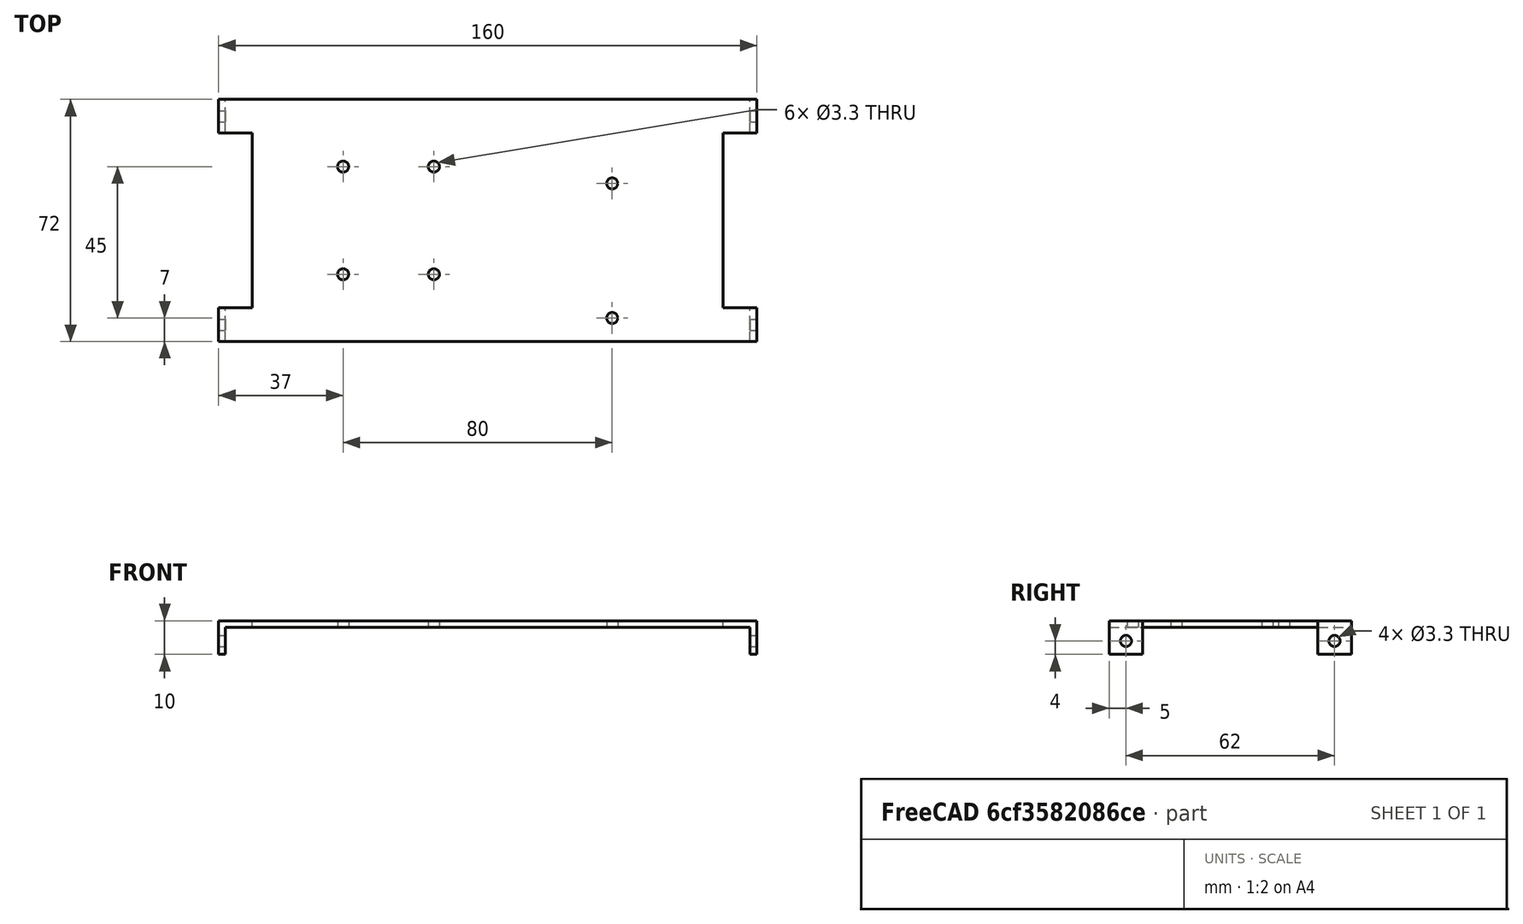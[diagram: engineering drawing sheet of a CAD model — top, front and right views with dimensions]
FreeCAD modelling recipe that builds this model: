
FCSTD DOCUMENT  (FreeCAD 0.17R13522 (Git))
Label: Zwischenblech_teensy
License: All rights reserved
LicenseURL: http://en.wikipedia.org/wiki/All_rights_reserved
objects: TechDraw::DrawViewDimension×22, Part::Box×3, Part::Cut×3, TechDraw::DrawProjGroupItem×3, Sketcher::SketchObject×2, PartDesign::Hole×2, Part::Mirroring×1, PartDesign::FeatureBase×1, TechDraw::DrawSVGTemplate×1, PartDesign::Body×1, TechDraw::DrawProjGroup×1, TechDraw::DrawPage×1
note: 15 computed .brp shape members not serialized (recipe doc carries the construction recipe); baked Part::Feature solids carry a one-line shape summary decoded from their .brp

FEATURE [Part::Box] Box  label="Würfel"
  AttacherType = Attacher::AttachEngine3D
  Height = 10
  Length = 160
  Width = 72
FEATURE [Part::Box] Box001  label="Würfel001"
  AttacherType = Attacher::AttachEngine3D
  Height = 10
  Length = 10
  Placement = pos=(0,10,0) rot=(0,0,1;0rad)
  Width = 52
FEATURE [Part::Mirroring] Part__Mirroring  label="Würfel001 (Mirror #1)"
  Base = (80,0,0)
  Normal = (1,0,0)
  Source = -> Box001
FEATURE [Part::Cut] Cut
  Base = -> Box
  Tool = -> Box001
FEATURE [Part::Cut] Cut001
  Base = -> Cut
  Tool = -> Part__Mirroring
FEATURE [Part::Box] Box002  label="Würfel002"
  AttacherType = Attacher::AttachEngine3D
  Height = 8
  Length = 156
  Placement = pos=(2,0,0) rot=(0,0,1;0rad)
  Width = 72
FEATURE [Part::Cut] Cut002
  Base = -> Cut001
  Tool = -> Box002
FEATURE [PartDesign::FeatureBase] BaseFeature
  BaseFeature = -> Cut002
FEATURE [Sketcher::SketchObject] Sketch
  MapMode = 5
  Placement = pos=(0,0,0) rot=(0.57735,-0.57735,-0.57735;2.0944rad)
  Support = -> [BaseFeature]
  sketch-geometry (2):
    g0: Circle CenterX=-5 CenterY=4 CenterZ=0 NormalX=0 NormalY=0 NormalZ=1 AngleXU=0 Radius=2.2
    g1: Circle CenterX=-67 CenterY=4 CenterZ=0 NormalX=0 NormalY=0 NormalZ=1 AngleXU=0 Radius=2.2
  constraints (6):
    c: Horizontal(g0,g1)
    c: DistanceY(g-1,g0) = 4
    c: Radius(g0) = 2.2
    c: Radius(g1) = 2.2
    c: DistanceX(g0,g-1) = 5
    c: DistanceX(g1,g-1) = 67
FEATURE [PartDesign::Hole] Hole
  BaseFeature = -> BaseFeature
  Depth = 25
  DepthType = 1
  Diameter = 3.3
  DrillPoint = 1
  DrillPointAngle = 118
  HoleCutCountersinkAngle = 90
  HoleCutDepth = 0
  HoleCutDiameter = 3
  HoleCutType = 0
  ModelActualThread = false
  Profile = -> Sketch
  Tapered = false
  TaperedAngle = 90
  ThreadAngle = 0
  ThreadClass = 0
  ThreadCutOffInner = 0
  ThreadCutOffOuter = 0
  ThreadDirection = 0
  ThreadFit = 0
  ThreadPitch = 0
  ThreadSize = 3
  ThreadType = 1
  Threaded = false
FEATURE [TechDraw::DrawSVGTemplate] Template
  EditableTexts = Designed_by_Name=Christian Dengler; FC-Date=25.04.2018; FC-SC=Scale; FC-SH=1/1; FC-Title=Zwischenblech, Mitte
  Height = 210
  Orientation = 1
  Width = 297
FEATURE [Sketcher::SketchObject] Sketch001
  MapMode = 5
  Placement = pos=(0,0,10) rot=(0,0,1;0rad)
  Support = -> [Hole]
  sketch-geometry (6):
    g0: Circle CenterX=37 CenterY=20 CenterZ=0 NormalX=0 NormalY=0 NormalZ=1 AngleXU=0 Radius=1.65
    g1: Circle CenterX=37 CenterY=52 CenterZ=0 NormalX=0 NormalY=0 NormalZ=1 AngleXU=0 Radius=1.65
    g2: Circle CenterX=64 CenterY=52 CenterZ=0 NormalX=0 NormalY=0 NormalZ=1 AngleXU=0 Radius=1.65
    g3: Circle CenterX=64 CenterY=20 CenterZ=0 NormalX=0 NormalY=0 NormalZ=1 AngleXU=0 Radius=1.65
    g4: Circle CenterX=117 CenterY=47 CenterZ=0 NormalX=0 NormalY=0 NormalZ=1 AngleXU=0 Radius=1.65
    g5: Circle CenterX=117 CenterY=7 CenterZ=0 NormalX=0 NormalY=0 NormalZ=1 AngleXU=0 Radius=1.65
  constraints (18):
    c: DistanceX(g-1,g0) = 37
    c: DistanceY(g-1,g0) = 20
    c: DistanceY(g0,g1) = 32
    c: DistanceX(g0,g3) = 27
    c: Vertical(g1,g0)
    c: Horizontal(g0,g3)
    c: Horizontal(g2,g1)
    c: Vertical(g2,g3)
    c: DistanceX(g3,g5) = 53
    c: Vertical(g5,g4)
    c: DistanceY(g5,g3) = 13
    c: DistanceY(g5,g4) = 40
    c: Radius(g1) = 1.65
    c: Radius(g0) = 1.65
    c: Radius(g2) = 1.65
    c: Radius(g3) = 1.65
    c: Radius(g4) = 1.65
    c: Radius(g5) = 1.65
FEATURE [PartDesign::Hole] Hole001
  BaseFeature = -> Hole
  Depth = 25
  DepthType = 1
  Diameter = 3.3
  DrillPoint = 1
  DrillPointAngle = 118
  HoleCutCountersinkAngle = 90
  HoleCutDepth = 0
  HoleCutDiameter = 3
  HoleCutType = 0
  ModelActualThread = false
  Profile = -> Sketch001
  Tapered = false
  TaperedAngle = 90
  ThreadAngle = 0
  ThreadClass = 0
  ThreadCutOffInner = 0
  ThreadCutOffOuter = 0
  ThreadDirection = 0
  ThreadFit = 0
  ThreadPitch = 0
  ThreadSize = 3
  ThreadType = 1
  Threaded = false
FEATURE [PartDesign::Body] Body
  BaseFeature = -> Cut002
  Group = -> [BaseFeature,Sketch,Hole,Sketch001,Hole001]
  Origin = -> Origin
  Tip = -> Hole001
FEATURE [TechDraw::DrawProjGroupItem] ProjItem  label="Front"
  CoarseView = false
  Direction = (0,-1,0)
  Focus = 100
  HardHidden = false
  IsoCount = 0
  IsoHidden = false
  IsoVisible = false
  LockPosition = false
  Perspective = false
  Rotation = 0
  RotationVector = (1,0,0)
  ScaleType = 0
  SeamHidden = false
  SeamVisible = false
  SmoothHidden = false
  SmoothVisible = false
  Source = -> [Body]
  Type = 0
  X = 0
  Y = 63.9337
FEATURE [TechDraw::DrawProjGroupItem] ProjItem001  label="Top"
  CoarseView = false
  Direction = (0,0,1)
  Focus = 100
  HardHidden = false
  IsoCount = 0
  IsoHidden = false
  IsoVisible = false
  LockPosition = false
  Perspective = false
  Rotation = 0
  RotationVector = (1,0,0)
  ScaleType = 0
  SeamHidden = false
  SeamVisible = false
  SmoothHidden = false
  SmoothVisible = false
  Source = -> [Body]
  Type = 4
  X = 0
  Y = -72.6
FEATURE [TechDraw::DrawProjGroupItem] ProjItem002  label="Left"
  CoarseView = false
  Direction = (-1,0,0)
  Focus = 100
  HardHidden = false
  IsoCount = 0
  IsoHidden = false
  IsoVisible = false
  LockPosition = true
  Perspective = false
  Rotation = 0
  RotationVector = (0,1,0)
  ScaleType = 0
  SeamHidden = false
  SeamVisible = false
  SmoothHidden = false
  SmoothVisible = false
  Source = -> [Body]
  Type = 1
  X = 132.721
  Y = 0
FEATURE [TechDraw::DrawProjGroup] ProjGroup
  Anchor = -> ProjItem
  AutoDistribute = true
  CubeDirs = (6) [(1.22465e-16,-2.44929e-16,-1),(1.93086e-32,-1,2.44929e-16),(-1,-2.46519e-32,-1.22465e-16),(-1.93086e-32,1,-2.44929e-16),(1,2.46519e-32,1.22465e-16),(-1.22465e-16,2.44929e-16,1)]
  CubeRotations = (6) [(1,2.46519e-32,1.22465e-16),(1,2.46519e-32,1.22465e-16),(4.89859e-16,1,-3.67394e-16),(-1,-2.46519e-32,-1.22465e-16),(-4.89859e-16,-1,3.67394e-16),(1,2.46519e-32,1.22465e-16)]
  LockPosition = false
  ProjectionType = 0
  Rotation = 0
  Scale = 0.8
  ScaleType = 2
  Source = -> [Body]
  Views = -> [ProjItem,ProjItem001,ProjItem002]
  X = 86.5544
  Y = 185.3
  spacingX = 15
  spacingY = 15
FEATURE [TechDraw::DrawViewDimension] Dimension
  FormatSpec = %.2f
  LockPosition = false
  MeasureType = 1
  References2D = -> [ProjItem002]
  Rotation = 0
  ScaleType = 0
  Type = 1
  X = 10.2351
  Y = -17.5972
FEATURE [TechDraw::DrawViewDimension] Dimension001
  FormatSpec = %.2f
  LockPosition = false
  MeasureType = 1
  References2D = -> [ProjItem002]
  Rotation = 0
  ScaleType = 0
  Type = 1
  X = -1.01532
  Y = -32.1706
FEATURE [TechDraw::DrawViewDimension] Dimension002
  FormatSpec = %.2f
  LockPosition = false
  MeasureType = 1
  References2D = -> [ProjItem002]
  Rotation = 0
  ScaleType = 0
  Type = 2
  X = 45.1628
  Y = -28.7923
FEATURE [TechDraw::DrawViewDimension] Dimension003
  FormatSpec = %.2f
  LockPosition = false
  MeasureType = 1
  References2D = -> [ProjItem002]
  Rotation = 0
  ScaleType = 0
  Type = 2
  X = 57.9248
  Y = -23.0222
FEATURE [TechDraw::DrawViewDimension] Dimension006
  FormatSpec = %.2f
  LockPosition = false
  MeasureType = 1
  References2D = -> [ProjItem001]
  Rotation = 0
  ScaleType = 0
  Type = 2
  X = 93.6457
  Y = 8.70013
FEATURE [TechDraw::DrawViewDimension] Dimension010
  FormatSpec = %.2f
  LockPosition = false
  MeasureType = 1
  References2D = -> [ProjItem]
  Rotation = 0
  ScaleType = 0
  Type = 1
  X = 50.0335
  Y = -8.66212
FEATURE [TechDraw::DrawViewDimension] Dimension011
  FormatSpec = %.2f
  LockPosition = false
  MeasureType = 1
  References2D = -> [ProjItem002]
  Rotation = 0
  ScaleType = 0
  Type = 5
  X = -52.7117
  Y = 9.58519
FEATURE [TechDraw::DrawViewDimension] Dimension012
  FormatSpec = %.2f
  LockPosition = false
  MeasureType = 1
  References2D = -> [ProjItem002]
  Rotation = 0
  ScaleType = 0
  Type = 1
  X = 2.22547
  Y = -24.7027
FEATURE [TechDraw::DrawViewDimension] Dimension013
  FormatSpec = %.2f
  LockPosition = false
  MeasureType = 1
  References2D = -> [ProjItem001]
  Rotation = 0
  ScaleType = 0
  Type = 2
  X = 84.3452
  Y = 8.90187
FEATURE [TechDraw::DrawViewDimension] Dimension014
  FormatSpec = %.2f
  LockPosition = false
  MeasureType = 1
  References2D = -> [ProjItem001]
  Rotation = 0
  ScaleType = 0
  Type = 2
  X = 103.707
  Y = 8.45678
FEATURE [TechDraw::DrawViewDimension] Dimension015
  FormatSpec = %.2f
  LockPosition = false
  MeasureType = 1
  References2D = -> [ProjItem001]
  Rotation = 0
  ScaleType = 0
  Type = 1
  X = 40.9486
  Y = 35.83
FEATURE [TechDraw::DrawViewDimension] Dimension016
  FormatSpec = %.2f
  LockPosition = false
  MeasureType = 1
  References2D = -> [ProjItem001]
  Rotation = 0
  ScaleType = 0
  Type = 1
  X = 34.4948
  Y = 44.9545
FEATURE [TechDraw::DrawViewDimension] Dimension017
  FormatSpec = %.2f
  LockPosition = false
  MeasureType = 1
  References2D = -> [ProjItem001]
  Rotation = 0
  ScaleType = 0
  Type = 1
  X = 19.8067
  Y = 52.9661
FEATURE [TechDraw::DrawViewDimension] Dimension018
  FormatSpec = %.2f
  LockPosition = false
  MeasureType = 1
  References2D = -> [ProjItem001]
  Rotation = 0
  ScaleType = 0
  Type = 1
  X = 44.2868
  Y = -33.6046
FEATURE [TechDraw::DrawViewDimension] Dimension022
  FormatSpec = %.2f
  LockPosition = false
  MeasureType = 1
  References2D = -> [ProjItem001]
  Rotation = 0
  ScaleType = 0
  Type = 2
  X = -44.0643
  Y = -48.2927
FEATURE [TechDraw::DrawViewDimension] Dimension023
  FormatSpec = %.2f
  LockPosition = false
  MeasureType = 1
  References2D = -> [ProjItem001]
  Rotation = 0
  ScaleType = 0
  Type = 2
  X = -52.2985
  Y = -53.8563
FEATURE [TechDraw::DrawViewDimension] Dimension024
  FormatSpec = %.2f
  LockPosition = false
  MeasureType = 1
  References2D = -> [ProjItem001]
  Rotation = 0
  ScaleType = 0
  Type = 1
  X = 18.9165
  Y = -45.177
FEATURE [TechDraw::DrawViewDimension] Dimension025
  FormatSpec = %.2f
  LockPosition = false
  MeasureType = 1
  References2D = -> [ProjItem001]
  Rotation = 0
  ScaleType = 0
  Type = 1
  X = 12.6852
  Y = -55.6367
FEATURE [TechDraw::DrawViewDimension] Dimension026
  FormatSpec = %.2f
  LockPosition = false
  MeasureType = 1
  References2D = -> [ProjItem001]
  Rotation = 0
  ScaleType = 0
  Type = 2
  X = 18.2488
  Y = -11.3499
FEATURE [TechDraw::DrawViewDimension] Dimension027
  FormatSpec = %.2f
  LockPosition = false
  MeasureType = 1
  References2D = -> [ProjItem001]
  Rotation = 0
  ScaleType = 0
  Type = 2
  X = 8.23423
  Y = -8.90187
FEATURE [TechDraw::DrawViewDimension] Dimension028
  FormatSpec = %.2f
  LockPosition = false
  MeasureType = 1
  References2D = -> [ProjItem001]
  Rotation = 0
  ScaleType = 0
  Type = 5
  X = -62.5357
  Y = 0.890187
FEATURE [TechDraw::DrawViewDimension] Dimension029
  FormatSpec = %.2f
  LockPosition = false
  MeasureType = 1
  References2D = -> [ProjItem001]
  Rotation = 0
  ScaleType = 0
  Type = 5
  X = -5.11858
  Y = 34.7173
FEATURE [TechDraw::DrawPage] Page
  KeepUpdated = true
  ProjectionType = 0
  Template = -> Template
  Views = -> [ProjGroup,Dimension,Dimension001,Dimension002,Dimension003,Dimension006,Dimension010,Dimension011,Dimension012,Dimension013,Dimension014,Dimension015,Dimension016,Dimension017,Dimension018,Dimension022,Dimension023,Dimension024,Dimension025,Dimension026,Dimension027,Dimension028,Dimension029]
